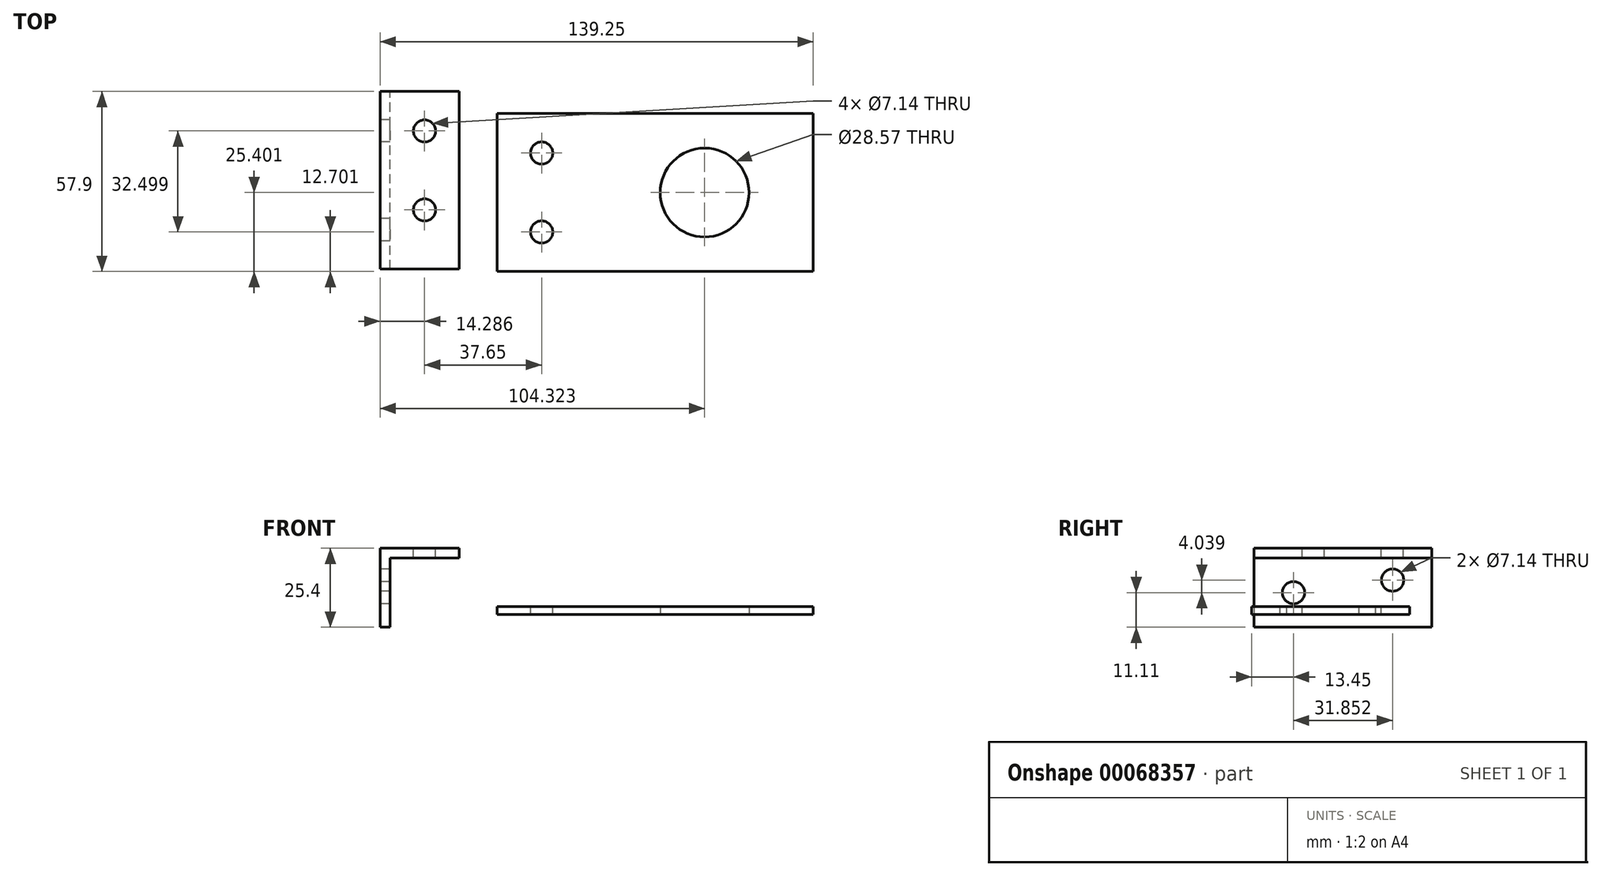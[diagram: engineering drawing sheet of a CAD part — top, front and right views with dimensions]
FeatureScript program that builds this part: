
annotation { "Feature Type Name" : "Feature", "Feature Type Description" : "" }
export const myFeature = defineFeature(function(context is Context, id is Id, definition is map)
    precondition{}
    {
        {
            var Q0;
            Q0=qCreatedBy(makeId("Top.planeOp"),FACE);
            var sketch = newSketch(context, id + "F0", { "sketchPlane" : qUnion([Q0])});
            skLineSegment(sketch, "E0.bottom", {"start": v(0.6, -7.1) * mm, "end": v(102.2, -7.1) * mm});
            skLineSegment(sketch, "E0.top", {"start": v(0.6, -57.9) * mm, "end": v(102.2, -57.9) * mm});
            skLineSegment(sketch, "E0.left", {"start": v(0.6, -7.1) * mm, "end": v(0.6, -57.9) * mm});
            skLineSegment(sketch, "E0.right", {"start": v(102.2, -7.1) * mm, "end": v(102.2, -57.9) * mm});
            skCircle(sketch, "E1", {"center": v(67.27, -32.5) * mm, "radius": 14.29 * mm});
            skSolve(sketch);
        }
        {
            var Q0;
            Q0 = qSketchRegion(id + "F0", true);
            extrude(context, id + "F1", {"entities" : qUnion([Q0]), "depth" : 2.54 * mm});
        }
        {
            var Q0;
            Q0=qCreatedBy(makeId("Front.planeOp"),FACE);
            var sketch = newSketch(context, id + "F2", { "sketchPlane" : qUnion([Q0])});
            skLineSegment(sketch, "E2.bottom", {"start": v(-37.05, 21.32) * mm, "end": v(-33.88, 21.32) * mm});
            skLineSegment(sketch, "E2.top", {"start": v(-37.05, -4.08) * mm, "end": v(-33.88, -4.08) * mm});
            skLineSegment(sketch, "E2.left", {"start": v(-37.05, 21.32) * mm, "end": v(-37.05, -4.08) * mm});
            skLineSegment(sketch, "E2.right", {"start": v(-33.88, 21.32) * mm, "end": v(-33.88, -4.08) * mm});
            skLineSegment(sketch, "E3.bottom", {"start": v(-37.05, 21.32) * mm, "end": v(-11.65, 21.32) * mm});
            skLineSegment(sketch, "E3.top", {"start": v(-37.05, 18.14) * mm, "end": v(-11.65, 18.14) * mm});
            skLineSegment(sketch, "E3.left", {"start": v(-37.05, 21.32) * mm, "end": v(-37.05, 18.14) * mm});
            skLineSegment(sketch, "E3.right", {"start": v(-11.65, 21.32) * mm, "end": v(-11.65, 18.14) * mm});
            skSolve(sketch);
        }
        {
            var Q0;
            Q0 = qSketchRegion(id + "F2", true);
            extrude(context, id + "F3", {"entities" : qUnion([Q0]), "depth" : 57.15 * mm});
        }
        {
            var Q0;
            Q0=makeQuery(id+"F3.opExtrude","SWEPT_FACE",FACE,{"disambiguationData":[OSD([sQuery(id+"F2.wireOp",EDGE,"E3.bottom")])]});
            var sketch = newSketch(context, id + "F4", { "sketchPlane" : qUnion([Q0])});
            skCircle(sketch, "E4", {"center": v(-22.76, -12.7) * mm, "radius": 3.57 * mm});
            skCircle(sketch, "E5", {"center": v(-22.76, -38.1) * mm, "radius": 3.57 * mm});
            skSolve(sketch);
        }
        {
            var Q0;
            Q0 = qSketchRegion(id + "F4", true);
            extrude(context, id + "F5", {"entities" : qUnion([Q0]), "operationType" : NewBodyOperationType.REMOVE, "oppositeDirection" : true, "depth" : 25.4 * mm});
        }
        {
            var Q0;
            Q0=makeQuery(id+"F1.opExtrude","CAP_FACE",FACE,{"disambiguationData":[OSD([sQuery(id+"F0.wireOp",EDGE,"E0.bottom"),sQuery(id+"F0.wireOp",EDGE,"E0.top"),sQuery(id+"F0.wireOp",EDGE,"E0.left"),sQuery(id+"F0.wireOp",EDGE,"E0.right"),sQuery(id+"F0.wireOp",EDGE,"E1")])],"isStart":false});
            var sketch = newSketch(context, id + "F6", { "sketchPlane" : qUnion([Q0])});
            skCircle(sketch, "E6", {"center": v(14.89, -19.8) * mm, "radius": 3.57 * mm});
            skCircle(sketch, "E7", {"center": v(14.89, -45.2) * mm, "radius": 3.57 * mm});
            skSolve(sketch);
        }
        {
            var Q0;
            Q0 = qSketchRegion(id + "F6", true);
            extrude(context, id + "F7", {"entities" : qUnion([Q0]), "operationType" : NewBodyOperationType.REMOVE, "oppositeDirection" : true, "depth" : 25.4 * mm});
        }
        {
            var Q0;
            Q0=makeQuery(id+"F3.opExtrude","SWEPT_FACE",FACE,{"disambiguationData":[OSD([sQuery(id+"F2.wireOp",EDGE,"E2.left"),sQuery(id+"F2.wireOp",EDGE,"E3.left")])]});
            var sketch = newSketch(context, id + "F8", { "sketchPlane" : qUnion([Q0])});
            skCircle(sketch, "E8", {"center": v(12.6, 11.07) * mm, "radius": 3.57 * mm});
            skCircle(sketch, "E9", {"center": v(44.45, 7.03) * mm, "radius": 3.57 * mm});
            skSolve(sketch);
        }
        {
            var Q0;
            Q0 = qSketchRegion(id + "F8", true);
            extrude(context, id + "F9", {"entities" : qUnion([Q0]), "operationType" : NewBodyOperationType.REMOVE, "oppositeDirection" : true, "depth" : 5.08 * mm});
        }
    });
